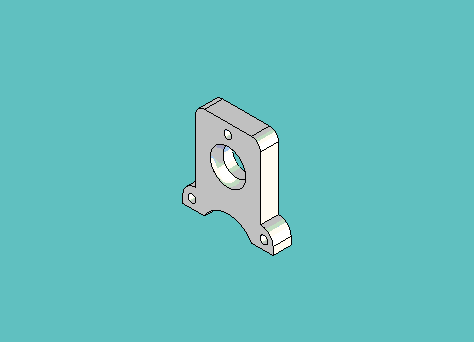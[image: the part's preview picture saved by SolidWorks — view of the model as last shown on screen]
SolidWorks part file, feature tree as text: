
SOLIDWORKS PART (.sldprt)
format: sldprt  version: not decoded by parser v0  size: 587,264 bytes
history: native  units: mm
features: sketch x4, cut_extrude x2, material x1, extrude x1, fillet x1, revolve x1, boolean_combine x1 (+11 scaffold rows collapsed)
feature tree (22):
  scaffold x11  (default folders/planes/origin — collapsed)
  material  "Material <not specified>"
  sketch  "Sketch1"  dims[c1.D1=7.9375mm c1.D4=9.525mm c1.D7=3.175mm c1.D8=4.445mm c2.D1=6.35mm c2.D2=14.732mm c2.D3=33.3375mm c3.D1=11.43mm c3.D2=19.05mm c3.D3=12.1285mm c3.D5=7.366mm c3.D6=15.875mm c3.D9=~4.66725mm c4.D1=19.05mm c4.D2=0.0mm]
  extrude  "Extrude1"  Depth=6.35mm
  fillet  "Fillet1"  Radius=2.38125mm
  sketch  "Sketch3"  dims[c1.D3=12.7mm c1.D1=14.2875mm c1.D2=11.684mm c2.D1=~0.79375mm]
  revolve  "Revolve1"  Angle=360deg
  boolean_combine  "Combine1"
  sketch  "Sketch4"  dims[D1=9.525mm]
  cut_extrude  "Cut-Extrude2"  [1 undecoded]
  sketch  "Sketch5"  dims[D1=3.048mm D2=3.048mm D3=3.2639mm]
  cut_extrude  "Cut-Extrude3"  [1 undecoded]
decode coverage: 7 of 10 modeling features carry decoded parameters
note: ~ marks probable driven/reference dimensions
note: 2 parameter values undecoded
note: suppression state not decoded; provenance and decode notes live in map.json
